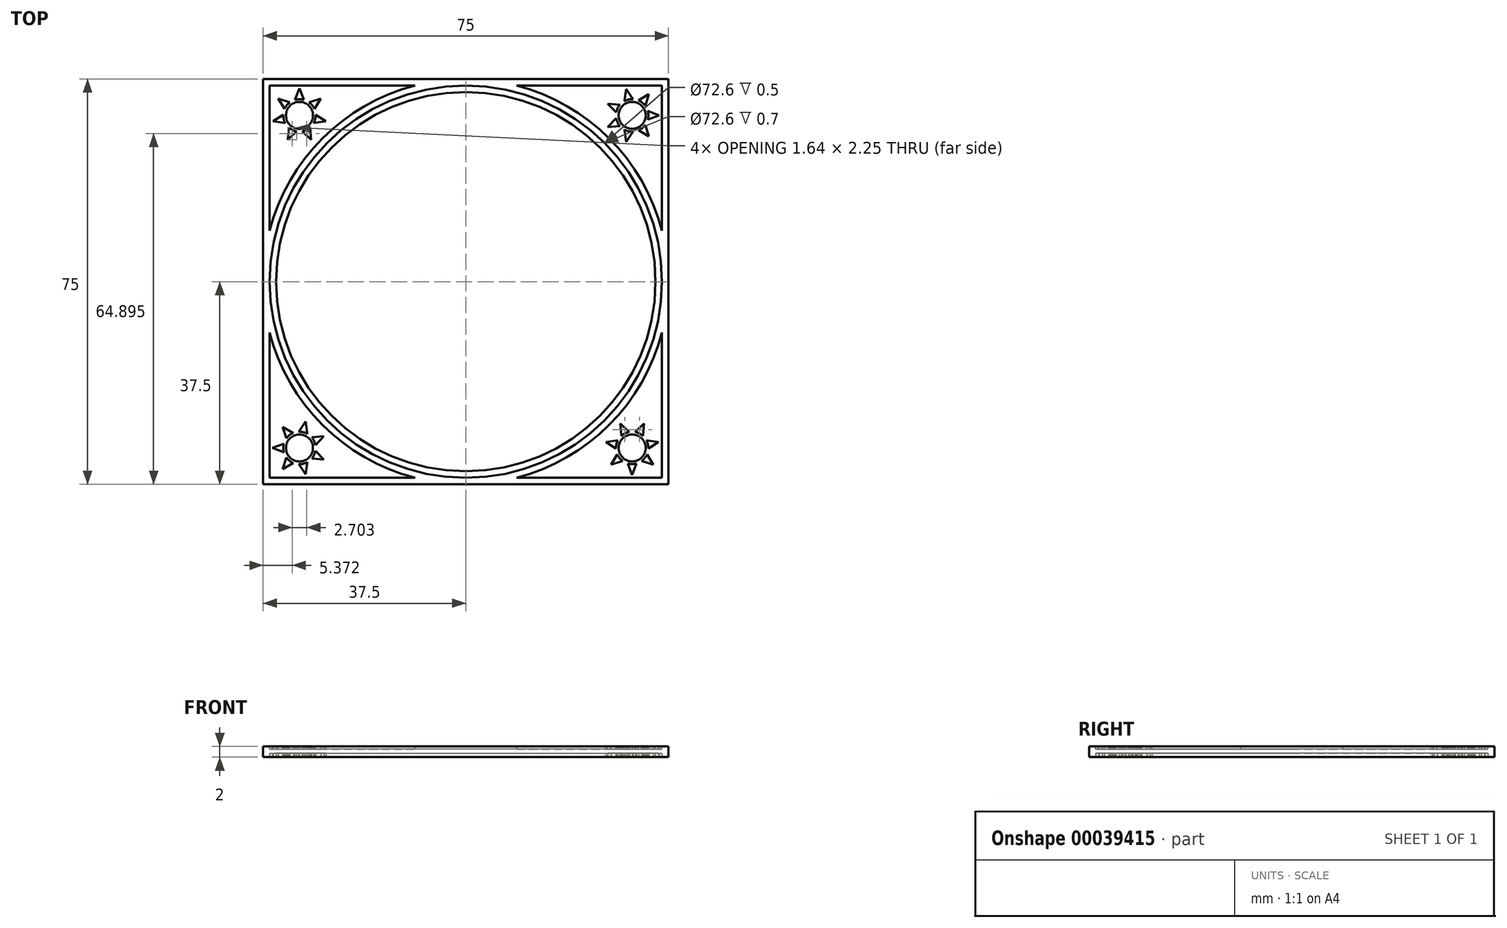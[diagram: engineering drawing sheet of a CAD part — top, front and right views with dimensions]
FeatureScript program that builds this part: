
annotation { "Feature Type Name" : "Feature", "Feature Type Description" : "" }
export const myFeature = defineFeature(function(context is Context, id is Id, definition is map)
    precondition{}
    {
        {
            var Q0;
            Q0=qCreatedBy(makeId("Top.planeOp"),FACE);
            var sketch = newSketch(context, id + "F0", { "sketchPlane" : qUnion([Q0])});
            skLineSegment(sketch, "E0.rect.bottom", {"start": v(37.5, -37.5) * mm, "end": v(-37.5, -37.5) * mm});
            skLineSegment(sketch, "E0.rect.top", {"start": v(37.5, 37.5) * mm, "end": v(-37.5, 37.5) * mm});
            skLineSegment(sketch, "E0.rect.left", {"start": v(37.5, -37.5) * mm, "end": v(37.5, 37.5) * mm});
            skLineSegment(sketch, "E0.rect.right", {"start": v(-37.5, -37.5) * mm, "end": v(-37.5, 37.5) * mm});
            skPoint(sketch, "E0.rect.middle", {"position": v(0, 0) * mm});
            skSolve(sketch);
        }
        {
            var Q0;
            Q0=qSketchRegion(id+"F0",true);
            extrude(context, id + "F1", {"entities" : qUnion([Q0]), "depth" : 2 * mm});
        }
        {
            var Q0;
            Q0=makeQuery(id+"F1.opExtrude","CAP_FACE",FACE,{"disambiguationData":[OSD([sQuery(id+"F0.wireOp",EDGE,"E0.rect.bottom"),sQuery(id+"F0.wireOp",EDGE,"E0.rect.top"),sQuery(id+"F0.wireOp",EDGE,"E0.rect.left"),sQuery(id+"F0.wireOp",EDGE,"E0.rect.right")])],"isStart":false});
            var sketch = newSketch(context, id + "F2", { "sketchPlane" : qUnion([Q0])});
            skLineSegment(sketch, "E1.rect.bottom", {"start": v(36.3, -36.3) * mm, "end": v(9.41, -36.3) * mm});
            skLineSegment(sketch, "E1.rect.top", {"start": v(36.3, 36.3) * mm, "end": v(9.41, 36.3) * mm});
            skLineSegment(sketch, "E1.rect.left", {"start": v(36.3, -36.3) * mm, "end": v(36.3, -9.41) * mm});
            skLineSegment(sketch, "E1.rect.right", {"start": v(-36.3, -36.3) * mm, "end": v(-36.3, -9.41) * mm});
            skPoint(sketch, "E1.rect.middle", {"position": v(0, 0) * mm});
            skCircle(sketch, "E2", {"center": v(0, 0) * mm, "radius": 35.1 * mm});
            skArc(sketch, "E3", {"start": v(-9.41, 36.3) * mm, "mid": v(-26.52, 26.52) * mm, "end": v(-36.3, 9.41) * mm});
            skArc(sketch, "E4.trimOffspring", {"start": v(36.3, 9.41) * mm, "mid": v(26.52, 26.52) * mm, "end": v(9.41, 36.3) * mm});
            skArc(sketch, "E5.trimOffspring", {"start": v(9.41, -36.3) * mm, "mid": v(26.52, -26.52) * mm, "end": v(36.3, -9.41) * mm});
            skArc(sketch, "E6.trimOffspring", {"start": v(-36.3, -9.41) * mm, "mid": v(-26.52, -26.52) * mm, "end": v(-9.41, -36.3) * mm});
            skLineSegment(sketch, "E7.trimOffspring", {"start": v(-36.3, 9.41) * mm, "end": v(-36.3, 36.3) * mm});
            skLineSegment(sketch, "E8.trimOffspring", {"start": v(-9.41, 36.3) * mm, "end": v(-36.3, 36.3) * mm});
            skLineSegment(sketch, "E9.trimOffspring", {"start": v(36.3, 9.41) * mm, "end": v(36.3, 36.3) * mm});
            skLineSegment(sketch, "E10.trimOffspring", {"start": v(-9.41, -36.3) * mm, "end": v(-36.3, -36.3) * mm});
            skCircle(sketch, "E11", {"center": v(0, 0) * mm, "radius": 36.3 * mm});
            skLineSegment(sketch, "E12", {"start": v(-36.3, 36.3) * mm, "end": v(-26.52, 26.52) * mm, "construction": true});
            skCircle(sketch, "E13", {"center": v(-30.78, 30.78) * mm, "radius": 2.5 * mm});
            skArc(sketch, "E14", {"start": v(-29.98, 33.67) * mm, "mid": v(-30.78, 33.78) * mm, "end": v(-31.58, 33.67) * mm});
            skLineSegment(sketch, "E15", {"start": v(-31.58, 33.67) * mm, "end": v(-30.78, 35.78) * mm});
            skLineSegment(sketch, "E16", {"start": v(-30.78, 35.78) * mm, "end": v(-29.98, 33.67) * mm});
            skArc(sketch, "E17.1.0", {"start": v(-32.54, 33.2) * mm, "mid": v(-33.12, 32.65) * mm, "end": v(-33.54, 31.95) * mm});
            skLineSegment(sketch, "E17.1.1", {"start": v(-34.69, 33.9) * mm, "end": v(-32.54, 33.2) * mm});
            skLineSegment(sketch, "E17.1.2", {"start": v(-33.54, 31.95) * mm, "end": v(-34.69, 33.9) * mm});
            skArc(sketch, "E17.2.0", {"start": v(-33.77, 30.91) * mm, "mid": v(-33.7, 30.1) * mm, "end": v(-33.42, 29.35) * mm});
            skLineSegment(sketch, "E17.2.1", {"start": v(-35.65, 29.66) * mm, "end": v(-33.77, 30.91) * mm});
            skLineSegment(sketch, "E17.2.2", {"start": v(-33.42, 29.35) * mm, "end": v(-35.65, 29.66) * mm});
            skArc(sketch, "E18.1.3.0", {"start": v(-32.75, 28.52) * mm, "mid": v(-32.08, 28.07) * mm, "end": v(-31.31, 27.82) * mm});
            skLineSegment(sketch, "E18.4.3.0", {"start": v(-32.95, 26.27) * mm, "end": v(-32.75, 28.52) * mm});
            skLineSegment(sketch, "E18.7.3.0", {"start": v(-31.31, 27.82) * mm, "end": v(-32.95, 26.27) * mm});
            skArc(sketch, "E18.1.4.0", {"start": v(-30.24, 27.82) * mm, "mid": v(-29.47, 28.07) * mm, "end": v(-28.8, 28.52) * mm});
            skLineSegment(sketch, "E18.4.4.0", {"start": v(-28.6, 26.27) * mm, "end": v(-30.24, 27.82) * mm});
            skLineSegment(sketch, "E18.7.4.0", {"start": v(-28.8, 28.52) * mm, "end": v(-28.6, 26.27) * mm});
            skArc(sketch, "E18.1.5.0", {"start": v(-28.14, 29.35) * mm, "mid": v(-27.85, 30.1) * mm, "end": v(-27.78, 30.91) * mm});
            skLineSegment(sketch, "E18.4.5.0", {"start": v(-25.9, 29.66) * mm, "end": v(-28.14, 29.35) * mm});
            skLineSegment(sketch, "E18.7.5.0", {"start": v(-27.78, 30.91) * mm, "end": v(-25.9, 29.66) * mm});
            skArc(sketch, "E18.1.6.0", {"start": v(-28.02, 31.95) * mm, "mid": v(-28.43, 32.65) * mm, "end": v(-29.01, 33.2) * mm});
            skLineSegment(sketch, "E18.4.6.0", {"start": v(-26.87, 33.9) * mm, "end": v(-28.02, 31.95) * mm});
            skLineSegment(sketch, "E18.7.6.0", {"start": v(-29.01, 33.2) * mm, "end": v(-26.87, 33.9) * mm});
            skCircle(sketch, "E19.1.0", {"center": v(-30.78, -30.78) * mm, "radius": 2.5 * mm});
            skArc(sketch, "E19.1.1", {"start": v(-33.67, -29.98) * mm, "mid": v(-33.78, -30.78) * mm, "end": v(-33.67, -31.58) * mm});
            skLineSegment(sketch, "E19.1.2", {"start": v(-33.67, -31.58) * mm, "end": v(-35.78, -30.78) * mm});
            skLineSegment(sketch, "E19.1.3", {"start": v(-35.78, -30.78) * mm, "end": v(-33.67, -29.98) * mm});
            skLineSegment(sketch, "E19.1.4", {"start": v(-33.2, -29.01) * mm, "end": v(-33.9, -26.87) * mm});
            skArc(sketch, "E19.1.5", {"start": v(-31.95, -28.02) * mm, "mid": v(-32.65, -28.43) * mm, "end": v(-33.2, -29.01) * mm});
            skLineSegment(sketch, "E19.1.6", {"start": v(-33.9, -26.87) * mm, "end": v(-31.95, -28.02) * mm});
            skLineSegment(sketch, "E19.1.7", {"start": v(-30.91, -27.78) * mm, "end": v(-29.66, -25.9) * mm});
            skArc(sketch, "E19.1.8", {"start": v(-29.35, -28.14) * mm, "mid": v(-30.1, -27.85) * mm, "end": v(-30.91, -27.78) * mm});
            skLineSegment(sketch, "E19.1.9", {"start": v(-29.66, -25.9) * mm, "end": v(-29.35, -28.14) * mm});
            skLineSegment(sketch, "E19.1.10", {"start": v(-28.52, -28.8) * mm, "end": v(-26.27, -28.6) * mm});
            skArc(sketch, "E19.1.11", {"start": v(-27.82, -30.24) * mm, "mid": v(-28.07, -29.47) * mm, "end": v(-28.52, -28.8) * mm});
            skLineSegment(sketch, "E19.1.12", {"start": v(-26.27, -28.6) * mm, "end": v(-27.82, -30.24) * mm});
            skLineSegment(sketch, "E19.1.13", {"start": v(-27.82, -31.31) * mm, "end": v(-26.27, -32.95) * mm});
            skArc(sketch, "E19.1.14", {"start": v(-28.52, -32.75) * mm, "mid": v(-28.07, -32.08) * mm, "end": v(-27.82, -31.31) * mm});
            skLineSegment(sketch, "E19.1.15", {"start": v(-26.27, -32.95) * mm, "end": v(-28.52, -32.75) * mm});
            skLineSegment(sketch, "E19.1.16", {"start": v(-29.35, -33.42) * mm, "end": v(-29.66, -35.65) * mm});
            skLineSegment(sketch, "E19.1.17", {"start": v(-29.66, -35.65) * mm, "end": v(-30.91, -33.77) * mm});
            skArc(sketch, "E19.1.18", {"start": v(-30.91, -33.77) * mm, "mid": v(-30.1, -33.7) * mm, "end": v(-29.35, -33.42) * mm});
            skLineSegment(sketch, "E19.1.19", {"start": v(-31.95, -33.54) * mm, "end": v(-33.9, -34.69) * mm});
            skLineSegment(sketch, "E19.1.20", {"start": v(-33.9, -34.69) * mm, "end": v(-33.2, -32.54) * mm});
            skArc(sketch, "E19.1.21", {"start": v(-33.2, -32.54) * mm, "mid": v(-32.65, -33.12) * mm, "end": v(-31.95, -33.54) * mm});
            skCircle(sketch, "E19.2.0", {"center": v(30.78, -30.78) * mm, "radius": 2.5 * mm});
            skArc(sketch, "E19.2.1", {"start": v(29.98, -33.67) * mm, "mid": v(30.78, -33.78) * mm, "end": v(31.58, -33.67) * mm});
            skLineSegment(sketch, "E19.2.2", {"start": v(31.58, -33.67) * mm, "end": v(30.78, -35.78) * mm});
            skLineSegment(sketch, "E19.2.3", {"start": v(30.78, -35.78) * mm, "end": v(29.98, -33.67) * mm});
            skLineSegment(sketch, "E19.2.4", {"start": v(29.01, -33.2) * mm, "end": v(26.87, -33.9) * mm});
            skArc(sketch, "E19.2.5", {"start": v(28.02, -31.95) * mm, "mid": v(28.43, -32.65) * mm, "end": v(29.01, -33.2) * mm});
            skLineSegment(sketch, "E19.2.6", {"start": v(26.87, -33.9) * mm, "end": v(28.02, -31.95) * mm});
            skLineSegment(sketch, "E19.2.7", {"start": v(27.78, -30.91) * mm, "end": v(25.9, -29.66) * mm});
            skArc(sketch, "E19.2.8", {"start": v(28.14, -29.35) * mm, "mid": v(27.85, -30.1) * mm, "end": v(27.78, -30.91) * mm});
            skLineSegment(sketch, "E19.2.9", {"start": v(25.9, -29.66) * mm, "end": v(28.14, -29.35) * mm});
            skLineSegment(sketch, "E19.2.10", {"start": v(28.8, -28.52) * mm, "end": v(28.6, -26.27) * mm});
            skArc(sketch, "E19.2.11", {"start": v(30.24, -27.82) * mm, "mid": v(29.47, -28.07) * mm, "end": v(28.8, -28.52) * mm});
            skLineSegment(sketch, "E19.2.12", {"start": v(28.6, -26.27) * mm, "end": v(30.24, -27.82) * mm});
            skLineSegment(sketch, "E19.2.13", {"start": v(31.31, -27.82) * mm, "end": v(32.95, -26.27) * mm});
            skArc(sketch, "E19.2.14", {"start": v(32.75, -28.52) * mm, "mid": v(32.08, -28.07) * mm, "end": v(31.31, -27.82) * mm});
            skLineSegment(sketch, "E19.2.15", {"start": v(32.95, -26.27) * mm, "end": v(32.75, -28.52) * mm});
            skLineSegment(sketch, "E19.2.16", {"start": v(33.42, -29.35) * mm, "end": v(35.65, -29.66) * mm});
            skLineSegment(sketch, "E19.2.17", {"start": v(35.65, -29.66) * mm, "end": v(33.77, -30.91) * mm});
            skArc(sketch, "E19.2.18", {"start": v(33.77, -30.91) * mm, "mid": v(33.7, -30.1) * mm, "end": v(33.42, -29.35) * mm});
            skLineSegment(sketch, "E19.2.19", {"start": v(33.54, -31.95) * mm, "end": v(34.69, -33.9) * mm});
            skLineSegment(sketch, "E19.2.20", {"start": v(34.69, -33.9) * mm, "end": v(32.54, -33.2) * mm});
            skArc(sketch, "E19.2.21", {"start": v(32.54, -33.2) * mm, "mid": v(33.12, -32.65) * mm, "end": v(33.54, -31.95) * mm});
            skCircle(sketch, "E20.1.3.0", {"center": v(30.78, 30.78) * mm, "radius": 2.5 * mm});
            skArc(sketch, "E20.2.3.0", {"start": v(33.67, 29.98) * mm, "mid": v(33.78, 30.78) * mm, "end": v(33.67, 31.58) * mm});
            skLineSegment(sketch, "E20.6.3.0", {"start": v(33.67, 31.58) * mm, "end": v(35.78, 30.78) * mm});
            skLineSegment(sketch, "E20.9.3.0", {"start": v(35.78, 30.78) * mm, "end": v(33.67, 29.98) * mm});
            skLineSegment(sketch, "E20.12.3.0", {"start": v(33.2, 29.01) * mm, "end": v(33.9, 26.87) * mm});
            skArc(sketch, "E20.15.3.0", {"start": v(31.95, 28.02) * mm, "mid": v(32.65, 28.43) * mm, "end": v(33.2, 29.01) * mm});
            skLineSegment(sketch, "E20.19.3.0", {"start": v(33.9, 26.87) * mm, "end": v(31.95, 28.02) * mm});
            skLineSegment(sketch, "E20.22.3.0", {"start": v(30.91, 27.78) * mm, "end": v(29.66, 25.9) * mm});
            skArc(sketch, "E20.25.3.0", {"start": v(29.35, 28.14) * mm, "mid": v(30.1, 27.85) * mm, "end": v(30.91, 27.78) * mm});
            skLineSegment(sketch, "E20.29.3.0", {"start": v(29.66, 25.9) * mm, "end": v(29.35, 28.14) * mm});
            skLineSegment(sketch, "E20.32.3.0", {"start": v(28.52, 28.8) * mm, "end": v(26.27, 28.6) * mm});
            skArc(sketch, "E20.35.3.0", {"start": v(27.82, 30.24) * mm, "mid": v(28.07, 29.47) * mm, "end": v(28.52, 28.8) * mm});
            skLineSegment(sketch, "E20.39.3.0", {"start": v(26.27, 28.6) * mm, "end": v(27.82, 30.24) * mm});
            skLineSegment(sketch, "E20.42.3.0", {"start": v(27.82, 31.31) * mm, "end": v(26.27, 32.95) * mm});
            skArc(sketch, "E20.45.3.0", {"start": v(28.52, 32.75) * mm, "mid": v(28.07, 32.08) * mm, "end": v(27.82, 31.31) * mm});
            skLineSegment(sketch, "E20.49.3.0", {"start": v(26.27, 32.95) * mm, "end": v(28.52, 32.75) * mm});
            skLineSegment(sketch, "E20.52.3.0", {"start": v(29.35, 33.42) * mm, "end": v(29.66, 35.65) * mm});
            skLineSegment(sketch, "E20.55.3.0", {"start": v(29.66, 35.65) * mm, "end": v(30.91, 33.77) * mm});
            skArc(sketch, "E20.58.3.0", {"start": v(30.91, 33.77) * mm, "mid": v(30.1, 33.7) * mm, "end": v(29.35, 33.42) * mm});
            skLineSegment(sketch, "E20.62.3.0", {"start": v(31.95, 33.54) * mm, "end": v(33.9, 34.69) * mm});
            skLineSegment(sketch, "E20.65.3.0", {"start": v(33.9, 34.69) * mm, "end": v(33.2, 32.54) * mm});
            skArc(sketch, "E20.68.3.0", {"start": v(33.2, 32.54) * mm, "mid": v(32.65, 33.12) * mm, "end": v(31.95, 33.54) * mm});
            skSolve(sketch);
        }
        {
            var Q0;
            Q0=qSketchRegion(id+"F2",true);
            extrude(context, id + "F3", {"entities" : qUnion([Q0]), "operationType" : NewBodyOperationType.REMOVE, "oppositeDirection" : true, "depth" : 0.5 * mm});
        }
        {
            var Q0;
            Q0=makeQuery(id+"F1.opExtrude","CAP_FACE",FACE,{"disambiguationData":[OSD([sQuery(id+"F0.wireOp",EDGE,"E0.rect.bottom"),sQuery(id+"F0.wireOp",EDGE,"E0.rect.top"),sQuery(id+"F0.wireOp",EDGE,"E0.rect.left"),sQuery(id+"F0.wireOp",EDGE,"E0.rect.right")])],"isStart":true});
            var sketch = newSketch(context, id + "F4", { "sketchPlane" : qUnion([Q0])});
            skLineSegment(sketch, "E21.0.0", {"start": v(29.98, 33.67) * mm, "end": v(30.78, 35.78) * mm});
            skLineSegment(sketch, "E21.0.1", {"start": v(30.78, 35.78) * mm, "end": v(31.58, 33.67) * mm});
            skArc(sketch, "E21.0.2", {"start": v(31.58, 33.67) * mm, "mid": v(30.78, 33.78) * mm, "end": v(29.98, 33.67) * mm});
            skArc(sketch, "E22.0.0", {"start": v(29.01, 33.2) * mm, "mid": v(28.43, 32.65) * mm, "end": v(28.02, 31.95) * mm});
            skLineSegment(sketch, "E22.0.1", {"start": v(28.02, 31.95) * mm, "end": v(26.87, 33.9) * mm});
            skLineSegment(sketch, "E22.0.2", {"start": v(26.87, 33.9) * mm, "end": v(29.01, 33.2) * mm});
            skArc(sketch, "E23.0.0", {"start": v(27.78, 30.91) * mm, "mid": v(27.85, 30.1) * mm, "end": v(28.14, 29.35) * mm});
            skLineSegment(sketch, "E23.0.1", {"start": v(28.14, 29.35) * mm, "end": v(25.9, 29.66) * mm});
            skLineSegment(sketch, "E23.0.2", {"start": v(25.9, 29.66) * mm, "end": v(27.78, 30.91) * mm});
            skArc(sketch, "E24.0.0", {"start": v(28.8, 28.52) * mm, "mid": v(29.47, 28.07) * mm, "end": v(30.24, 27.82) * mm});
            skLineSegment(sketch, "E24.0.1", {"start": v(30.24, 27.82) * mm, "end": v(28.6, 26.27) * mm});
            skLineSegment(sketch, "E24.0.2", {"start": v(28.6, 26.27) * mm, "end": v(28.8, 28.52) * mm});
            skArc(sketch, "E25.0.0", {"start": v(31.31, 27.82) * mm, "mid": v(32.08, 28.07) * mm, "end": v(32.75, 28.52) * mm});
            skLineSegment(sketch, "E25.0.1", {"start": v(32.75, 28.52) * mm, "end": v(32.95, 26.27) * mm});
            skLineSegment(sketch, "E25.0.2", {"start": v(32.95, 26.27) * mm, "end": v(31.31, 27.82) * mm});
            skArc(sketch, "E26.0.0", {"start": v(33.42, 29.35) * mm, "mid": v(33.7, 30.1) * mm, "end": v(33.77, 30.91) * mm});
            skLineSegment(sketch, "E26.0.1", {"start": v(33.77, 30.91) * mm, "end": v(35.65, 29.66) * mm});
            skLineSegment(sketch, "E26.0.2", {"start": v(35.65, 29.66) * mm, "end": v(33.42, 29.35) * mm});
            skArc(sketch, "E27.0.0", {"start": v(33.54, 31.95) * mm, "mid": v(33.12, 32.65) * mm, "end": v(32.54, 33.2) * mm});
            skLineSegment(sketch, "E27.0.1", {"start": v(32.54, 33.2) * mm, "end": v(34.69, 33.9) * mm});
            skLineSegment(sketch, "E27.0.2", {"start": v(34.69, 33.9) * mm, "end": v(33.54, 31.95) * mm});
            skArc(sketch, "E28.0.0", {"start": v(-29.35, 33.42) * mm, "mid": v(-30.1, 33.7) * mm, "end": v(-30.91, 33.77) * mm});
            skLineSegment(sketch, "E28.0.1", {"start": v(-30.91, 33.77) * mm, "end": v(-29.66, 35.65) * mm});
            skLineSegment(sketch, "E28.0.2", {"start": v(-29.66, 35.65) * mm, "end": v(-29.35, 33.42) * mm});
            skArc(sketch, "E29.0.0", {"start": v(-31.95, 33.54) * mm, "mid": v(-32.65, 33.12) * mm, "end": v(-33.2, 32.54) * mm});
            skLineSegment(sketch, "E29.0.1", {"start": v(-33.2, 32.54) * mm, "end": v(-33.9, 34.69) * mm});
            skLineSegment(sketch, "E29.0.2", {"start": v(-33.9, 34.69) * mm, "end": v(-31.95, 33.54) * mm});
            skLineSegment(sketch, "E30.0.0", {"start": v(-33.67, 29.98) * mm, "end": v(-35.78, 30.78) * mm});
            skLineSegment(sketch, "E30.0.1", {"start": v(-35.78, 30.78) * mm, "end": v(-33.67, 31.58) * mm});
            skArc(sketch, "E30.0.2", {"start": v(-33.67, 31.58) * mm, "mid": v(-33.78, 30.78) * mm, "end": v(-33.67, 29.98) * mm});
            skLineSegment(sketch, "E31.0", {"start": v(-33.9, 26.87) * mm, "end": v(-31.95, 28.02) * mm});
            skArc(sketch, "E32.0.0", {"start": v(-33.2, 29.01) * mm, "mid": v(-32.65, 28.43) * mm, "end": v(-31.95, 28.02) * mm});
            skLineSegment(sketch, "E32.0.1", {"start": v(-31.95, 28.02) * mm, "end": v(-33.9, 26.87) * mm});
            skLineSegment(sketch, "E32.0.2", {"start": v(-33.9, 26.87) * mm, "end": v(-33.2, 29.01) * mm});
            skArc(sketch, "E33.0.0", {"start": v(-30.91, 27.78) * mm, "mid": v(-30.1, 27.85) * mm, "end": v(-29.35, 28.14) * mm});
            skLineSegment(sketch, "E33.0.1", {"start": v(-29.35, 28.14) * mm, "end": v(-29.66, 25.9) * mm});
            skLineSegment(sketch, "E33.0.2", {"start": v(-29.66, 25.9) * mm, "end": v(-30.91, 27.78) * mm});
            skArc(sketch, "E34.0.0", {"start": v(-28.52, 28.8) * mm, "mid": v(-28.07, 29.47) * mm, "end": v(-27.82, 30.24) * mm});
            skLineSegment(sketch, "E34.0.1", {"start": v(-27.82, 30.24) * mm, "end": v(-26.27, 28.6) * mm});
            skLineSegment(sketch, "E34.0.2", {"start": v(-26.27, 28.6) * mm, "end": v(-28.52, 28.8) * mm});
            skArc(sketch, "E35.0.0", {"start": v(-27.82, 31.31) * mm, "mid": v(-28.07, 32.08) * mm, "end": v(-28.52, 32.75) * mm});
            skLineSegment(sketch, "E35.0.1", {"start": v(-28.52, 32.75) * mm, "end": v(-26.27, 32.95) * mm});
            skLineSegment(sketch, "E35.0.2", {"start": v(-26.27, 32.95) * mm, "end": v(-27.82, 31.31) * mm});
            skLineSegment(sketch, "E36.0.0", {"start": v(-30.24, -27.82) * mm, "end": v(-28.6, -26.27) * mm});
            skLineSegment(sketch, "E36.0.1", {"start": v(-28.6, -26.27) * mm, "end": v(-28.8, -28.52) * mm});
            skArc(sketch, "E36.0.2", {"start": v(-28.8, -28.52) * mm, "mid": v(-29.47, -28.07) * mm, "end": v(-30.24, -27.82) * mm});
            skLineSegment(sketch, "E37.0.0", {"start": v(-32.75, -28.52) * mm, "end": v(-32.95, -26.27) * mm});
            skLineSegment(sketch, "E37.0.1", {"start": v(-32.95, -26.27) * mm, "end": v(-31.31, -27.82) * mm});
            skArc(sketch, "E37.0.2", {"start": v(-31.31, -27.82) * mm, "mid": v(-32.08, -28.07) * mm, "end": v(-32.75, -28.52) * mm});
            skLineSegment(sketch, "E38.0.0", {"start": v(-33.77, -30.91) * mm, "end": v(-35.65, -29.66) * mm});
            skLineSegment(sketch, "E38.0.1", {"start": v(-35.65, -29.66) * mm, "end": v(-33.42, -29.35) * mm});
            skArc(sketch, "E38.0.2", {"start": v(-33.42, -29.35) * mm, "mid": v(-33.7, -30.1) * mm, "end": v(-33.77, -30.91) * mm});
            skLineSegment(sketch, "E39.0.0", {"start": v(-32.54, -33.2) * mm, "end": v(-34.69, -33.9) * mm});
            skLineSegment(sketch, "E39.0.1", {"start": v(-34.69, -33.9) * mm, "end": v(-33.54, -31.95) * mm});
            skArc(sketch, "E39.0.2", {"start": v(-33.54, -31.95) * mm, "mid": v(-33.12, -32.65) * mm, "end": v(-32.54, -33.2) * mm});
            skLineSegment(sketch, "E40.0.0", {"start": v(-29.98, -33.67) * mm, "end": v(-30.78, -35.78) * mm});
            skLineSegment(sketch, "E40.0.1", {"start": v(-30.78, -35.78) * mm, "end": v(-31.58, -33.67) * mm});
            skArc(sketch, "E40.0.2", {"start": v(-31.58, -33.67) * mm, "mid": v(-30.78, -33.78) * mm, "end": v(-29.98, -33.67) * mm});
            skLineSegment(sketch, "E41.0.0", {"start": v(-28.02, -31.95) * mm, "end": v(-26.87, -33.9) * mm});
            skLineSegment(sketch, "E41.0.1", {"start": v(-26.87, -33.9) * mm, "end": v(-29.01, -33.2) * mm});
            skArc(sketch, "E41.0.2", {"start": v(-29.01, -33.2) * mm, "mid": v(-28.43, -32.65) * mm, "end": v(-28.02, -31.95) * mm});
            skLineSegment(sketch, "E42.0.0", {"start": v(-28.14, -29.35) * mm, "end": v(-25.9, -29.66) * mm});
            skLineSegment(sketch, "E42.0.1", {"start": v(-25.9, -29.66) * mm, "end": v(-27.78, -30.91) * mm});
            skArc(sketch, "E42.0.2", {"start": v(-27.78, -30.91) * mm, "mid": v(-27.85, -30.1) * mm, "end": v(-28.14, -29.35) * mm});
            skArc(sketch, "E43.0.0", {"start": v(30.91, -27.78) * mm, "mid": v(30.1, -27.85) * mm, "end": v(29.35, -28.14) * mm});
            skLineSegment(sketch, "E43.0.1", {"start": v(29.35, -28.14) * mm, "end": v(29.66, -25.9) * mm});
            skLineSegment(sketch, "E43.0.2", {"start": v(29.66, -25.9) * mm, "end": v(30.91, -27.78) * mm});
            skArc(sketch, "E44.0.0", {"start": v(28.52, -28.8) * mm, "mid": v(28.07, -29.47) * mm, "end": v(27.82, -30.24) * mm});
            skLineSegment(sketch, "E44.0.1", {"start": v(27.82, -30.24) * mm, "end": v(26.27, -28.6) * mm});
            skLineSegment(sketch, "E44.0.2", {"start": v(26.27, -28.6) * mm, "end": v(28.52, -28.8) * mm});
            skArc(sketch, "E45.0.0", {"start": v(27.82, -31.31) * mm, "mid": v(28.07, -32.08) * mm, "end": v(28.52, -32.75) * mm});
            skLineSegment(sketch, "E45.0.1", {"start": v(28.52, -32.75) * mm, "end": v(26.27, -32.95) * mm});
            skLineSegment(sketch, "E45.0.2", {"start": v(26.27, -32.95) * mm, "end": v(27.82, -31.31) * mm});
            skArc(sketch, "E46.0.0", {"start": v(29.35, -33.42) * mm, "mid": v(30.1, -33.7) * mm, "end": v(30.91, -33.77) * mm});
            skLineSegment(sketch, "E46.0.1", {"start": v(30.91, -33.77) * mm, "end": v(29.66, -35.65) * mm});
            skLineSegment(sketch, "E46.0.2", {"start": v(29.66, -35.65) * mm, "end": v(29.35, -33.42) * mm});
            skArc(sketch, "E47.0.0", {"start": v(31.95, -33.54) * mm, "mid": v(32.65, -33.12) * mm, "end": v(33.2, -32.54) * mm});
            skLineSegment(sketch, "E47.0.1", {"start": v(33.2, -32.54) * mm, "end": v(33.9, -34.69) * mm});
            skLineSegment(sketch, "E47.0.2", {"start": v(33.9, -34.69) * mm, "end": v(31.95, -33.54) * mm});
            skLineSegment(sketch, "E48.0.0", {"start": v(33.67, -29.98) * mm, "end": v(35.78, -30.78) * mm});
            skLineSegment(sketch, "E48.0.1", {"start": v(35.78, -30.78) * mm, "end": v(33.67, -31.58) * mm});
            skArc(sketch, "E48.0.2", {"start": v(33.67, -31.58) * mm, "mid": v(33.78, -30.78) * mm, "end": v(33.67, -29.98) * mm});
            skArc(sketch, "E49.0.0", {"start": v(33.2, -29.01) * mm, "mid": v(32.65, -28.43) * mm, "end": v(31.95, -28.02) * mm});
            skLineSegment(sketch, "E49.0.1", {"start": v(31.95, -28.02) * mm, "end": v(33.9, -26.87) * mm});
            skLineSegment(sketch, "E49.0.2", {"start": v(33.9, -26.87) * mm, "end": v(33.2, -29.01) * mm});
            skCircle(sketch, "E50.0.0", {"center": v(0, 0) * mm, "radius": 36.3 * mm});
            skCircle(sketch, "E51.0.0", {"center": v(0, 0) * mm, "radius": 35.1 * mm});
            skSolve(sketch);
        }
        {
            var Q0;
            Q0=qSketchRegion(id+"F4",true);
            extrude(context, id + "F5", {"entities" : qUnion([Q0]), "operationType" : NewBodyOperationType.REMOVE, "oppositeDirection" : true, "depth" : .7 * mm});
        }
    });
